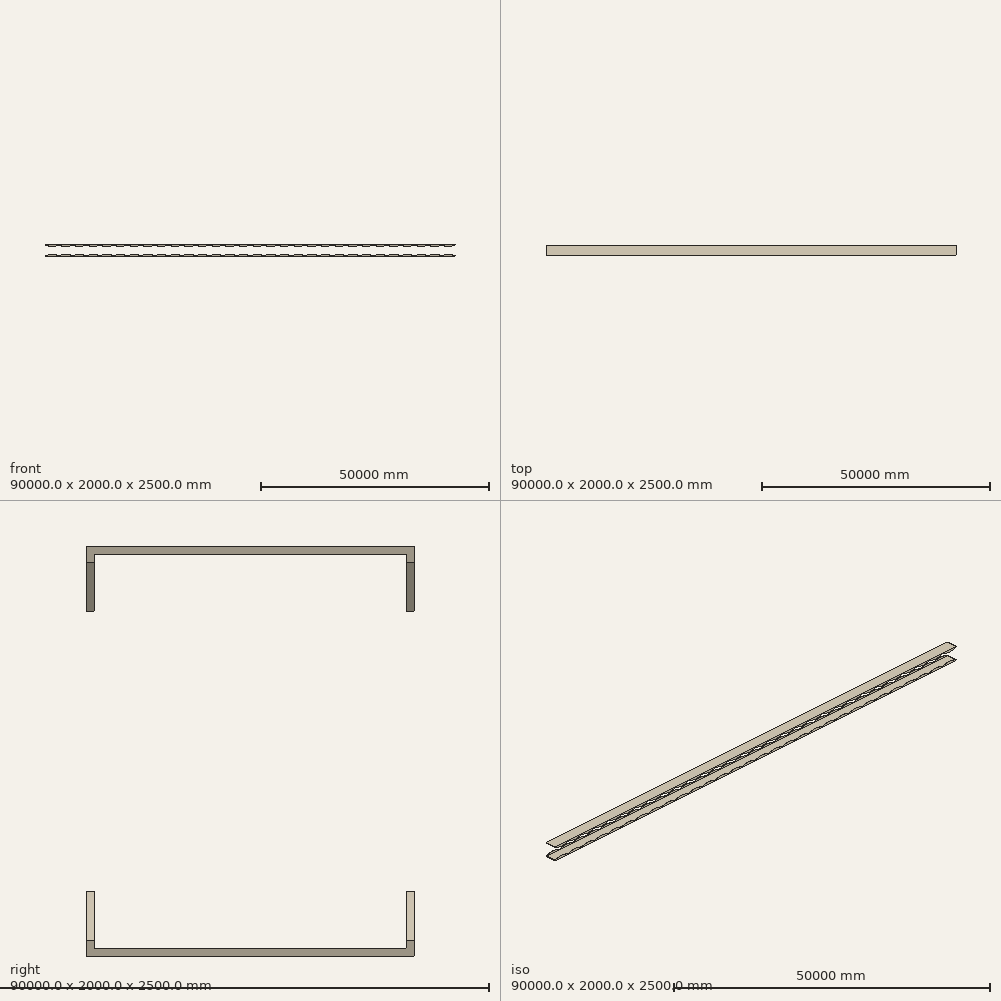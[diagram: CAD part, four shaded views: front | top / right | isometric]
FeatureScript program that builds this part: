
annotation { "Feature Type Name" : "Feature", "Feature Type Description" : "" }
export const myFeature = defineFeature(function(context is Context, id is Id, definition is map)
    precondition{}
    {
        {
            var Q0;
            Q0=qCreatedBy(makeId("Top.planeOp"),FACE);
            var sketch = newSketch(context, id + "F0", { "sketchPlane" : qUnion([Q0])});
            skLineSegment(sketch, "E0.bottom", {"start": v(-90000, 2034.95) * mm, "end": v(0, 2034.95) * mm});
            skLineSegment(sketch, "E0.top", {"start": v(-90000, 34.95) * mm, "end": v(0, 34.95) * mm});
            skLineSegment(sketch, "E0.left", {"start": v(-90000, 2034.95) * mm, "end": v(-90000, 34.95) * mm});
            skLineSegment(sketch, "E0.right", {"start": v(0, 2034.95) * mm, "end": v(0, 34.95) * mm});
            skSolve(sketch);
        }
        {
            var Q0;
            Q0=makeQuery(id+"F0.imprint","IMPRINT",FACE,{"disambiguationData":[TD([[makeQuery(id+"F0.imprint","IMPRINT",EDGE,{"derivedFrom":sQuery(id+"F0.wireOp",EDGE,"E0.bottom")}),-1.0]])]});
            extrude(context, id + "F1", {"entities" : qUnion([Q0]), "depth" : 2500 * mm, "offsetDistance" : 25 * mm});
        }
        {
            var Q0;
            Q0=makeQuery(id+"F1.opExtrude","SWEPT_FACE",FACE,{"disambiguationData":[OSD([sQuery(id+"F0.wireOp",EDGE,"E0.right")])]});
            var sketch = newSketch(context, id + "F2", { "sketchPlane" : qUnion([Q0])});
            skLineSegment(sketch, "E1.bottom", {"start": v(1984.95, 50) * mm, "end": v(84.95, 50) * mm});
            skLineSegment(sketch, "E1.top", {"start": v(1984.95, 2450) * mm, "end": v(84.95, 2450) * mm});
            skLineSegment(sketch, "E1.left", {"start": v(1984.95, 50) * mm, "end": v(1984.95, 2450) * mm});
            skLineSegment(sketch, "E1.right", {"start": v(84.95, 50) * mm, "end": v(84.95, 2450) * mm});
            skSolve(sketch);
        }
        {
            var Q0;
            Q0=makeQuery(id+"F2.imprint","IMPRINT",FACE,{"disambiguationData":[TD([[makeQuery(id+"F2.imprint","IMPRINT",EDGE,{"derivedFrom":sQuery(id+"F2.wireOp",EDGE,"E1.bottom")}),-1.0]])]});
            extrude(context, id + "F3", {"entities" : qUnion([Q0]), "operationType" : NewBodyOperationType.REMOVE, "oppositeDirection" : true, "depth" : 90000 * mm, "offsetDistance" : 25 * mm});
        }
        {
            var Q0;
            Q0=makeQuery(id+"F1.opExtrude","SWEPT_FACE",FACE,{"disambiguationData":[OSD([sQuery(id+"F0.wireOp",EDGE,"E0.top")])]});
            var sketch = newSketch(context, id + "F4", { "sketchPlane" : qUnion([Q0])});
            skLineSegment(sketch, "E2", {"start": v(-90000, 0) * mm, "end": v(-90000, 400) * mm});
            skPoint(sketch, "E3", {"position": v(-88500, 0) * mm});
            skFitSpline(sketch, "E4", {"points": [v(-90000, 100) * mm, v(-88500, 400) * mm, v(-87000, 100) * mm], "startDerivative": vector(3000, 900) * mm, "endDerivative": vector(3000, -900) * mm});
            skFitSpline(sketch, "E5", {"points": [v(-87000, 100) * mm, v(-85500, 400) * mm, v(-84000, 100) * mm], "startDerivative": vector(3000, 900) * mm, "endDerivative": vector(3000, -900) * mm});
            skFitSpline(sketch, "E6", {"points": [v(-84000, 100) * mm, v(-82500, 400) * mm, v(-81000, 100) * mm], "startDerivative": vector(3000, 900) * mm, "endDerivative": vector(3000, -900) * mm});
            skFitSpline(sketch, "E7", {"points": [v(-81000, 100) * mm, v(-79500, 400) * mm, v(-78000, 100) * mm], "startDerivative": vector(3000, 900) * mm, "endDerivative": vector(3000, -900) * mm});
            skFitSpline(sketch, "E8", {"points": [v(-78000, 100) * mm, v(-76500, 400) * mm, v(-75000, 100) * mm], "startDerivative": vector(3000, 900) * mm, "endDerivative": vector(3000, -900) * mm});
            skFitSpline(sketch, "E9", {"points": [v(-75000, 100) * mm, v(-73500, 400) * mm, v(-72000, 100) * mm], "startDerivative": vector(3000, 900) * mm, "endDerivative": vector(3000, -900) * mm});
            skFitSpline(sketch, "E10", {"points": [v(-72000, 100) * mm, v(-70500, 400) * mm, v(-69000, 100) * mm], "startDerivative": vector(3000, 900) * mm, "endDerivative": vector(3000, -900) * mm});
            skFitSpline(sketch, "E11", {"points": [v(-69000, 100) * mm, v(-67500, 400) * mm, v(-66000, 100) * mm], "startDerivative": vector(3000, 900) * mm, "endDerivative": vector(3000, -900) * mm});
            skFitSpline(sketch, "E12", {"points": [v(-66000, 100) * mm, v(-64500, 400) * mm, v(-63000, 100) * mm], "startDerivative": vector(3000, 900) * mm, "endDerivative": vector(3000, -900) * mm});
            skFitSpline(sketch, "E13", {"points": [v(-63000, 100) * mm, v(-61500, 400) * mm, v(-60000, 100) * mm], "startDerivative": vector(3000, 900) * mm, "endDerivative": vector(3000, -900) * mm});
            skFitSpline(sketch, "E14", {"points": [v(-60000, 100) * mm, v(-58500, 400) * mm, v(-57000, 100) * mm], "startDerivative": vector(3000, 900) * mm, "endDerivative": vector(3000, -900) * mm});
            skFitSpline(sketch, "E15", {"points": [v(-57000, 100) * mm, v(-55500, 400) * mm, v(-54000, 100) * mm], "startDerivative": vector(3000, 900) * mm, "endDerivative": vector(3000, -900) * mm});
            skFitSpline(sketch, "E16", {"points": [v(-54000, 100) * mm, v(-52500, 400) * mm, v(-51000, 100) * mm], "startDerivative": vector(3000, 900) * mm, "endDerivative": vector(3000, -900) * mm});
            skFitSpline(sketch, "E17", {"points": [v(-51000, 100) * mm, v(-49500, 400) * mm, v(-48000, 100) * mm], "startDerivative": vector(3000, 900) * mm, "endDerivative": vector(3000, -900) * mm});
            skFitSpline(sketch, "E18", {"points": [v(-48000, 100) * mm, v(-46500, 400) * mm, v(-45000, 100) * mm], "startDerivative": vector(3000, 900) * mm, "endDerivative": vector(3000, -900) * mm});
            skFitSpline(sketch, "E19", {"points": [v(-45000, 100) * mm, v(-43500, 400) * mm, v(-42000, 100) * mm], "startDerivative": vector(3000, 900) * mm, "endDerivative": vector(3000, -900) * mm});
            skFitSpline(sketch, "E20", {"points": [v(-42000, 100) * mm, v(-40500, 400) * mm, v(-39000, 100) * mm], "startDerivative": vector(3000, 900) * mm, "endDerivative": vector(3000, -900) * mm});
            skFitSpline(sketch, "E21", {"points": [v(-39000, 100) * mm, v(-37500, 400) * mm, v(-36000, 100) * mm], "startDerivative": vector(3000, 900) * mm, "endDerivative": vector(3000, -900) * mm});
            skFitSpline(sketch, "E22", {"points": [v(-36000, 100) * mm, v(-34500, 400) * mm, v(-33000, 100) * mm], "startDerivative": vector(3000, 900) * mm, "endDerivative": vector(3000, -900) * mm});
            skFitSpline(sketch, "E23", {"points": [v(-33000, 100) * mm, v(-31500, 400) * mm, v(-30000, 100) * mm], "startDerivative": vector(3000, 900) * mm, "endDerivative": vector(3000, -900) * mm});
            skFitSpline(sketch, "E24", {"points": [v(-30000, 100) * mm, v(-28500, 400) * mm, v(-27000, 100) * mm], "startDerivative": vector(3000, 900) * mm, "endDerivative": vector(3000, -900) * mm});
            skFitSpline(sketch, "E25", {"points": [v(-27000, 100) * mm, v(-25500, 400) * mm, v(-24000, 100) * mm], "startDerivative": vector(3000, 900) * mm, "endDerivative": vector(3000, -900) * mm});
            skFitSpline(sketch, "E26", {"points": [v(-24000, 100) * mm, v(-22500, 400) * mm, v(-21000, 100) * mm], "startDerivative": vector(3000, 900) * mm, "endDerivative": vector(3000, -900) * mm});
            skFitSpline(sketch, "E27", {"points": [v(-21000, 100) * mm, v(-19500, 400) * mm, v(-18000, 100) * mm], "startDerivative": vector(3000, 900) * mm, "endDerivative": vector(3000, -900) * mm});
            skFitSpline(sketch, "E28", {"points": [v(-18000, 100) * mm, v(-16500, 400) * mm, v(-15000, 100) * mm], "startDerivative": vector(3000, 900) * mm, "endDerivative": vector(3000, -900) * mm});
            skFitSpline(sketch, "E29", {"points": [v(-15000, 100) * mm, v(-13500, 400) * mm, v(-12000, 100) * mm], "startDerivative": vector(3000, 900) * mm, "endDerivative": vector(3000, -900) * mm});
            skFitSpline(sketch, "E30", {"points": [v(-12000, 100) * mm, v(-10500, 400) * mm, v(-9000, 100) * mm], "startDerivative": vector(3000, 900) * mm, "endDerivative": vector(3000, -900) * mm});
            skFitSpline(sketch, "E31", {"points": [v(-9000, 100) * mm, v(-7500, 400) * mm, v(-6000, 100) * mm], "startDerivative": vector(3000, 900) * mm, "endDerivative": vector(3000, -900) * mm});
            skFitSpline(sketch, "E32", {"points": [v(-6000, 100) * mm, v(-4500, 400) * mm, v(-3000, 100) * mm], "startDerivative": vector(3000, 900) * mm, "endDerivative": vector(3000, -900) * mm});
            skFitSpline(sketch, "E33", {"points": [v(-3000, 100) * mm, v(-1500, 400) * mm, v(0, 100) * mm], "startDerivative": vector(3000, 900) * mm, "endDerivative": vector(3000, -900) * mm});
            skFitSpline(sketch, "E34.MirrorCS", {"points": [v(-90000, 2400) * mm, v(-88500, 2100) * mm, v(-87000, 2400) * mm], "startDerivative": vector(3000, -900) * mm, "endDerivative": vector(3000, 900) * mm});
            skFitSpline(sketch, "E35.MirrorCS", {"points": [v(-87000, 2400) * mm, v(-85500, 2100) * mm, v(-84000, 2400) * mm], "startDerivative": vector(3000, -900) * mm, "endDerivative": vector(3000, 900) * mm});
            skFitSpline(sketch, "E36.MirrorCS", {"points": [v(-84000, 2400) * mm, v(-82500, 2100) * mm, v(-81000, 2400) * mm], "startDerivative": vector(3000, -900) * mm, "endDerivative": vector(3000, 900) * mm});
            skFitSpline(sketch, "E37.MirrorCS", {"points": [v(-81000, 2400) * mm, v(-79500, 2100) * mm, v(-78000, 2400) * mm], "startDerivative": vector(3000, -900) * mm, "endDerivative": vector(3000, 900) * mm});
            skFitSpline(sketch, "E38.MirrorCS", {"points": [v(-78000, 2400) * mm, v(-76500, 2100) * mm, v(-75000, 2400) * mm], "startDerivative": vector(3000, -900) * mm, "endDerivative": vector(3000, 900) * mm});
            skFitSpline(sketch, "E39.MirrorCS", {"points": [v(-75000, 2400) * mm, v(-73500, 2100) * mm, v(-72000, 2400) * mm], "startDerivative": vector(3000, -900) * mm, "endDerivative": vector(3000, 900) * mm});
            skFitSpline(sketch, "E40.MirrorCS", {"points": [v(-72000, 2400) * mm, v(-70500, 2100) * mm, v(-69000, 2400) * mm], "startDerivative": vector(3000, -900) * mm, "endDerivative": vector(3000, 900) * mm});
            skFitSpline(sketch, "E41.MirrorCS", {"points": [v(-69000, 2400) * mm, v(-67500, 2100) * mm, v(-66000, 2400) * mm], "startDerivative": vector(3000, -900) * mm, "endDerivative": vector(3000, 900) * mm});
            skFitSpline(sketch, "E42.MirrorCS", {"points": [v(-66000, 2400) * mm, v(-64500, 2100) * mm, v(-63000, 2400) * mm], "startDerivative": vector(3000, -900) * mm, "endDerivative": vector(3000, 900) * mm});
            skFitSpline(sketch, "E43.MirrorCS", {"points": [v(-63000, 2400) * mm, v(-61500, 2100) * mm, v(-60000, 2400) * mm], "startDerivative": vector(3000, -900) * mm, "endDerivative": vector(3000, 900) * mm});
            skFitSpline(sketch, "E44.MirrorCS", {"points": [v(-60000, 2400) * mm, v(-58500, 2100) * mm, v(-57000, 2400) * mm], "startDerivative": vector(3000, -900) * mm, "endDerivative": vector(3000, 900) * mm});
            skFitSpline(sketch, "E45.MirrorCS", {"points": [v(-57000, 2400) * mm, v(-55500, 2100) * mm, v(-54000, 2400) * mm], "startDerivative": vector(3000, -900) * mm, "endDerivative": vector(3000, 900) * mm});
            skFitSpline(sketch, "E46.MirrorCS", {"points": [v(-54000, 2400) * mm, v(-52500, 2100) * mm, v(-51000, 2400) * mm], "startDerivative": vector(3000, -900) * mm, "endDerivative": vector(3000, 900) * mm});
            skFitSpline(sketch, "E47.MirrorCS", {"points": [v(-51000, 2400) * mm, v(-49500, 2100) * mm, v(-48000, 2400) * mm], "startDerivative": vector(3000, -900) * mm, "endDerivative": vector(3000, 900) * mm});
            skFitSpline(sketch, "E48.MirrorCS", {"points": [v(-48000, 2400) * mm, v(-46500, 2100) * mm, v(-45000, 2400) * mm], "startDerivative": vector(3000, -900) * mm, "endDerivative": vector(3000, 900) * mm});
            skFitSpline(sketch, "E49.MirrorCS", {"points": [v(-45000, 2400) * mm, v(-43500, 2100) * mm, v(-42000, 2400) * mm], "startDerivative": vector(3000, -900) * mm, "endDerivative": vector(3000, 900) * mm});
            skFitSpline(sketch, "E50.MirrorCS", {"points": [v(-42000, 2400) * mm, v(-40500, 2100) * mm, v(-39000, 2400) * mm], "startDerivative": vector(3000, -900) * mm, "endDerivative": vector(3000, 900) * mm});
            skFitSpline(sketch, "E51.MirrorCS", {"points": [v(-39000, 2400) * mm, v(-37500, 2100) * mm, v(-36000, 2400) * mm], "startDerivative": vector(3000, -900) * mm, "endDerivative": vector(3000, 900) * mm});
            skFitSpline(sketch, "E52.MirrorCS", {"points": [v(-36000, 2400) * mm, v(-34500, 2100) * mm, v(-33000, 2400) * mm], "startDerivative": vector(3000, -900) * mm, "endDerivative": vector(3000, 900) * mm});
            skFitSpline(sketch, "E53.MirrorCS", {"points": [v(-33000, 2400) * mm, v(-31500, 2100) * mm, v(-30000, 2400) * mm], "startDerivative": vector(3000, -900) * mm, "endDerivative": vector(3000, 900) * mm});
            skFitSpline(sketch, "E54.MirrorCS", {"points": [v(-30000, 2400) * mm, v(-28500, 2100) * mm, v(-27000, 2400) * mm], "startDerivative": vector(3000, -900) * mm, "endDerivative": vector(3000, 900) * mm});
            skFitSpline(sketch, "E55.MirrorCS", {"points": [v(-27000, 2400) * mm, v(-25500, 2100) * mm, v(-24000, 2400) * mm], "startDerivative": vector(3000, -900) * mm, "endDerivative": vector(3000, 900) * mm});
            skFitSpline(sketch, "E56.MirrorCS", {"points": [v(-24000, 2400) * mm, v(-22500, 2100) * mm, v(-21000, 2400) * mm], "startDerivative": vector(3000, -900) * mm, "endDerivative": vector(3000, 900) * mm});
            skFitSpline(sketch, "E57.MirrorCS", {"points": [v(-21000, 2400) * mm, v(-19500, 2100) * mm, v(-18000, 2400) * mm], "startDerivative": vector(3000, -900) * mm, "endDerivative": vector(3000, 900) * mm});
            skFitSpline(sketch, "E58.MirrorCS", {"points": [v(-18000, 2400) * mm, v(-16500, 2100) * mm, v(-15000, 2400) * mm], "startDerivative": vector(3000, -900) * mm, "endDerivative": vector(3000, 900) * mm});
            skFitSpline(sketch, "E59.MirrorCS", {"points": [v(-15000, 2400) * mm, v(-13500, 2100) * mm, v(-12000, 2400) * mm], "startDerivative": vector(3000, -900) * mm, "endDerivative": vector(3000, 900) * mm});
            skFitSpline(sketch, "E60.MirrorCS", {"points": [v(-12000, 2400) * mm, v(-10500, 2100) * mm, v(-9000, 2400) * mm], "startDerivative": vector(3000, -900) * mm, "endDerivative": vector(3000, 900) * mm});
            skFitSpline(sketch, "E61.MirrorCS", {"points": [v(-9000, 2400) * mm, v(-7500, 2100) * mm, v(-6000, 2400) * mm], "startDerivative": vector(3000, -900) * mm, "endDerivative": vector(3000, 900) * mm});
            skFitSpline(sketch, "E62.MirrorCS", {"points": [v(-6000, 2400) * mm, v(-4500, 2100) * mm, v(-3000, 2400) * mm], "startDerivative": vector(3000, -900) * mm, "endDerivative": vector(3000, 900) * mm});
            skFitSpline(sketch, "E63.MirrorCS", {"points": [v(-3000, 2400) * mm, v(-1500, 2100) * mm, v(0, 2400) * mm], "startDerivative": vector(3000, -900) * mm, "endDerivative": vector(3000, 900) * mm});
            skSolve(sketch);
        }
        {
            var Q0;
            {var subQ6=sQuery(id+"F4.wireOp",EDGE,"E4");Q0=makeQuery(id+"F4.imprint","IMPRINT",FACE,{"disambiguationData":[TD([[makeQuery(id+"F4.imprint","IMPRINT",EDGE,{"derivedFrom":subQ6}),1.0]])]});}
            extrude(context, id + "F5", {"entities" : qUnion([Q0]), "operationType" : NewBodyOperationType.REMOVE, "oppositeDirection" : true, "depth" : 2000 * mm, "offsetDistance" : 25 * mm});
        }
    });
